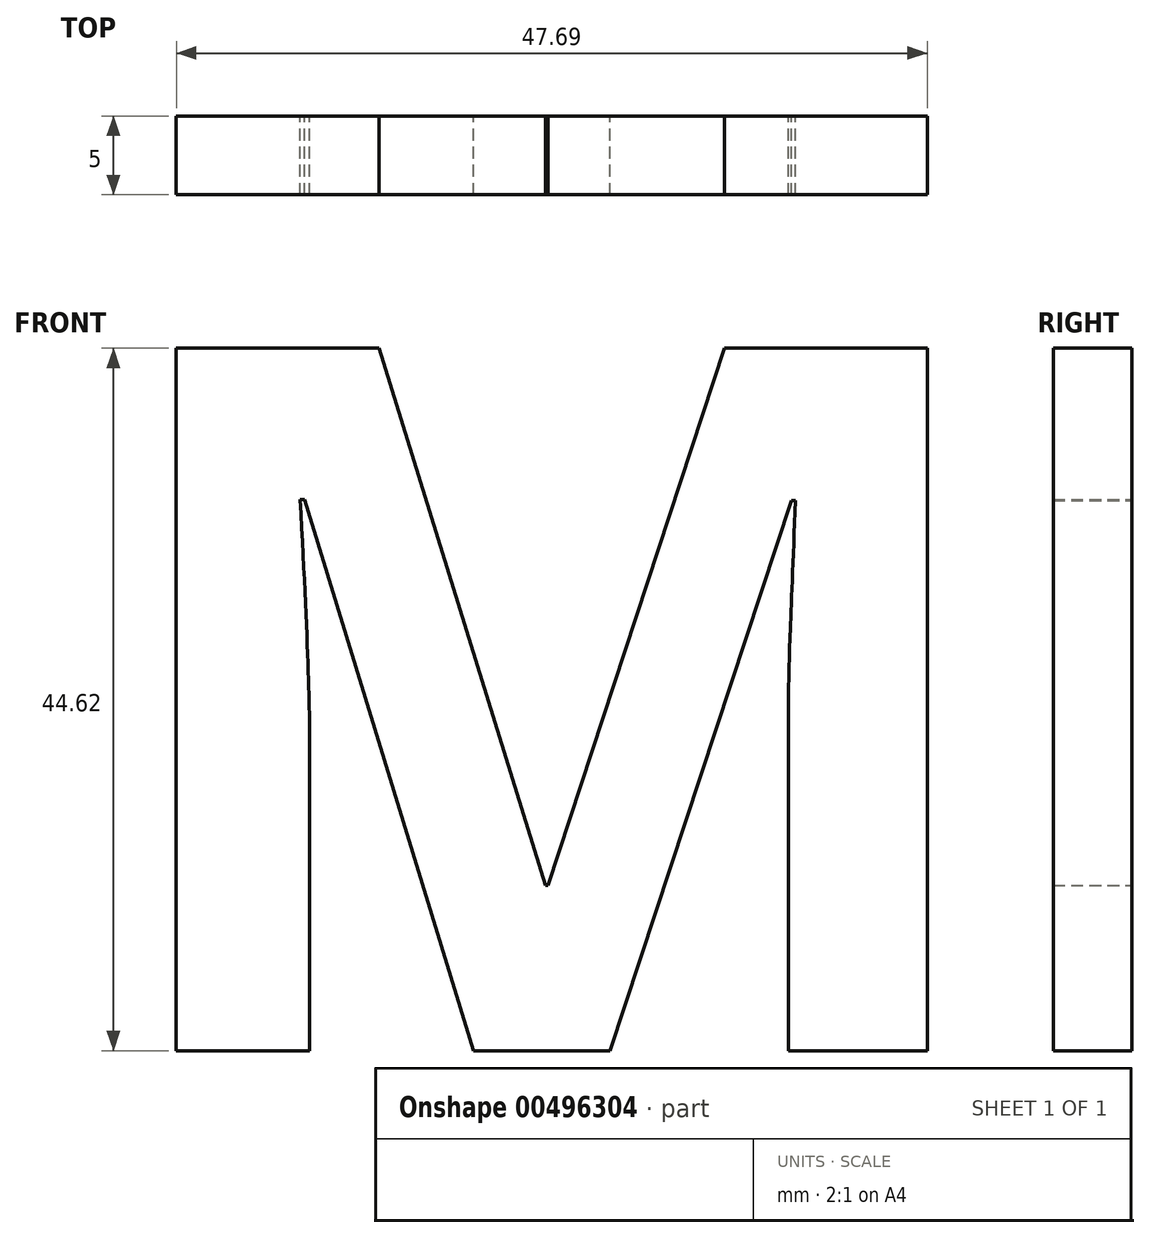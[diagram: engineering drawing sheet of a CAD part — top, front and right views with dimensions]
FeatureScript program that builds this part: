
annotation { "Feature Type Name" : "Feature", "Feature Type Description" : "" }
export const myFeature = defineFeature(function(context is Context, id is Id, definition is map)
    precondition{}
    {
        {
            var Q0;
            Q0=qCreatedBy(makeId("Front.planeOp"),FACE);
            var sketch = newSketch(context, id + "F0", { "sketchPlane" : qUnion([Q0])});
            skText(sketch, "E0", { "text": "M", "fontName": "OpenSans-Bold.ttf"});
            const initialGuessF0  = {"E0": [-0.06518, 0.0159, 1, 0, 0.045]};
            skSetInitialGuess(sketch, initialGuessF0);
            skSolve(sketch);
        }
        {
            var Q0;
            Q0=makeQuery(id+"F0.imprint","IMPRINT",FACE,{"disambiguationData":[TD([[makeQuery(id+"F0.imprint","IMPRINT",EDGE,{"derivedFrom":sQuery(id+"F0.wireOp",EDGE,"E0.sketch_text.stroke-0")}),-1.0]])]});
            extrude(context, id + "F1", {"entities" : qUnion([Q0]), "depth" : 5 * mm});
        }
    });
